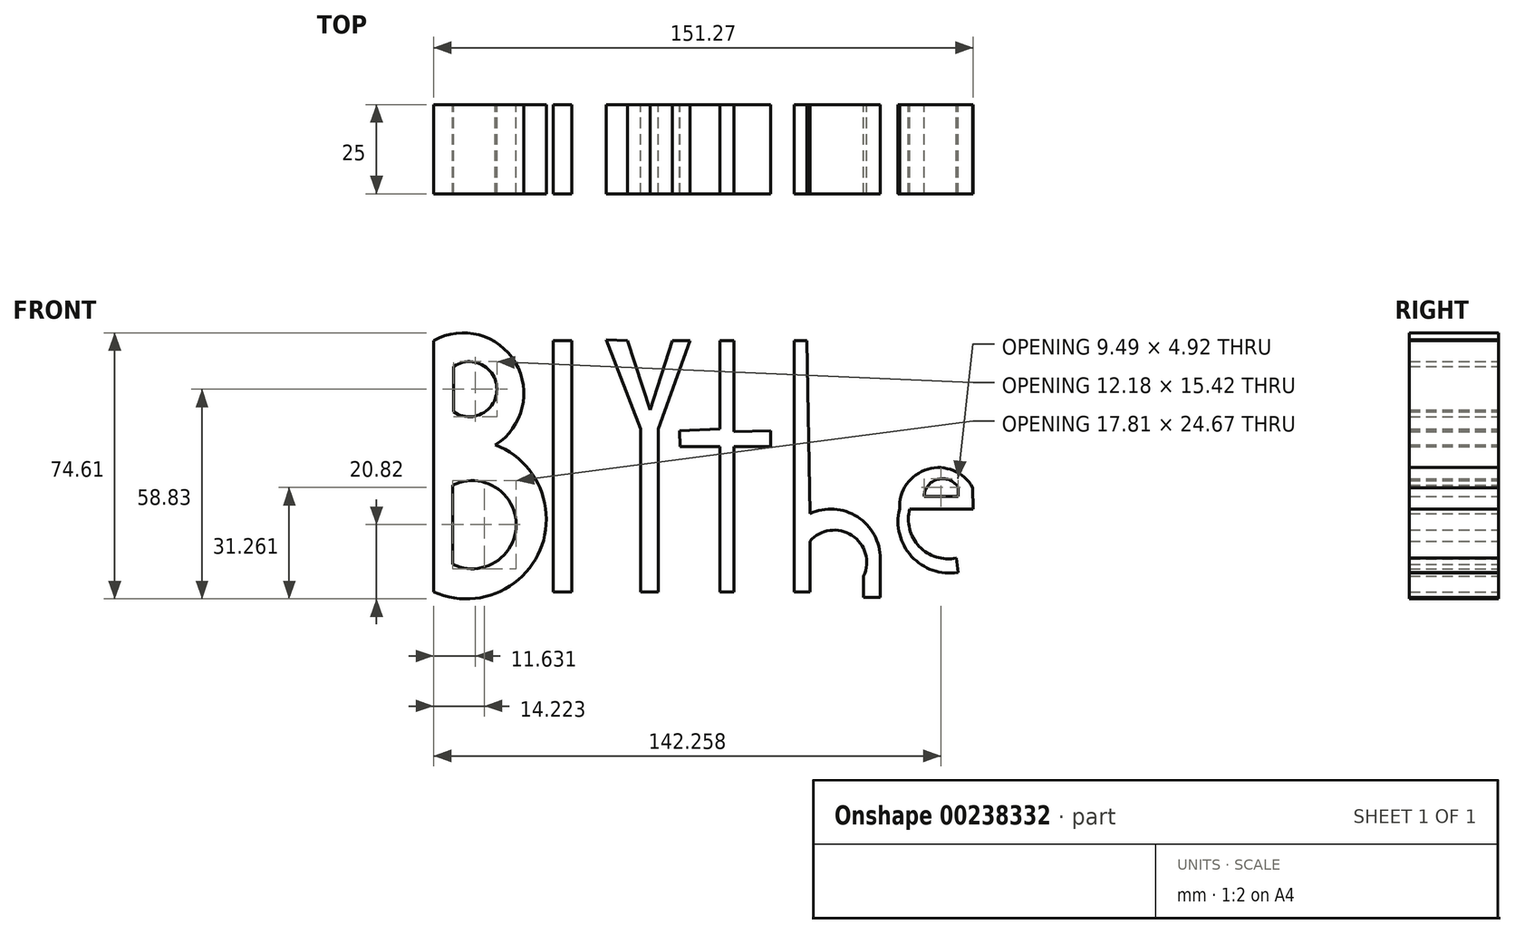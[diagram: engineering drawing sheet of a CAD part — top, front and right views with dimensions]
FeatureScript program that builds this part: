
annotation { "Feature Type Name" : "Feature", "Feature Type Description" : "" }
export const myFeature = defineFeature(function(context is Context, id is Id, definition is map)
    precondition{}
    {
        {
            var Q0;
            Q0=qCreatedBy(makeId("Front.planeOp"),FACE);
            var sketch = newSketch(context, id + "F0", { "sketchPlane" : qUnion([Q0])});
            skLineSegment(sketch, "E0", {"start": v(-71.8, 43.66) * mm, "end": v(-71.8, -26.82) * mm});
            skArc(sketch, "E1", {"start": v(-71.8, -26.82) * mm, "mid": v(-40.23, -6.43) * mm, "end": v(-71.8, 13.96) * mm});
            skArc(sketch, "E2", {"start": v(-71.8, 13.96) * mm, "mid": v(-46.53, 28.81) * mm, "end": v(-71.8, 43.66) * mm});
            skLineSegment(sketch, "E3", {"start": v(-66.27, 36.35) * mm, "end": v(-66.27, 23.71) * mm});
            skArc(sketch, "E4", {"start": v(-66.27, 23.71) * mm, "mid": v(-54.09, 30.03) * mm, "end": v(-66.27, 36.35) * mm});
            skLineSegment(sketch, "E5", {"start": v(-66.5, 3.1) * mm, "end": v(-66.5, -19.06) * mm});
            skArc(sketch, "E6", {"start": v(-66.5, -19.06) * mm, "mid": v(-48.68, -7.98) * mm, "end": v(-66.5, 3.1) * mm});
            skLineSegment(sketch, "E7", {"start": v(-38.34, 43.66) * mm, "end": v(-38.34, -26.82) * mm});
            skLineSegment(sketch, "E8", {"start": v(-38.34, -26.82) * mm, "end": v(-33.02, -26.82) * mm});
            skLineSegment(sketch, "E9", {"start": v(-33.02, -26.82) * mm, "end": v(-33.02, 43.66) * mm});
            skLineSegment(sketch, "E10", {"start": v(-33.02, 43.66) * mm, "end": v(-38.34, 43.66) * mm});
            skLineSegment(sketch, "E11", {"start": v(-17.5, 43.66) * mm, "end": v(-23.46, 43.94) * mm});
            skPoint(sketch, "E11.startSnap0", {"position": v(-35.68, 43.66) * mm});
            skLineSegment(sketch, "E12", {"start": v(-23.46, 43.94) * mm, "end": v(-13.74, 18.84) * mm});
            skLineSegment(sketch, "E13", {"start": v(-13.74, 18.84) * mm, "end": v(-13.74, -26.82) * mm});
            skLineSegment(sketch, "E14", {"start": v(-13.74, -26.82) * mm, "end": v(-8.87, -26.82) * mm});
            skLineSegment(sketch, "E15", {"start": v(-8.87, -26.82) * mm, "end": v(-8.87, 18.84) * mm});
            skLineSegment(sketch, "E16", {"start": v(-8.87, 18.84) * mm, "end": v(0, 43.66) * mm});
            skLineSegment(sketch, "E17", {"start": v(0, 43.66) * mm, "end": v(-4.88, 43.66) * mm});
            skLineSegment(sketch, "E18", {"start": v(-4.88, 43.66) * mm, "end": v(-11.08, 24.16) * mm});
            skLineSegment(sketch, "E19", {"start": v(-11.08, 24.16) * mm, "end": v(-17.5, 43.66) * mm});
            skLineSegment(sketch, "E20", {"start": v(8.42, 43.66) * mm, "end": v(8.42, 18.84) * mm});
            skLineSegment(sketch, "E21", {"start": v(8.42, 18.84) * mm, "end": v(-2.87, 18.38) * mm});
            skLineSegment(sketch, "E22", {"start": v(-2.87, 18.38) * mm, "end": v(-2.7, 13.95) * mm});
            skLineSegment(sketch, "E23", {"start": v(-2.7, 13.95) * mm, "end": v(8.42, 13.95) * mm});
            skLineSegment(sketch, "E24", {"start": v(8.42, 13.95) * mm, "end": v(8.42, -26.82) * mm});
            skLineSegment(sketch, "E25", {"start": v(8.42, -26.82) * mm, "end": v(12.41, -26.82) * mm});
            skLineSegment(sketch, "E26", {"start": v(12.41, -26.82) * mm, "end": v(12.41, 13.95) * mm});
            skLineSegment(sketch, "E27", {"start": v(12.41, 13.95) * mm, "end": v(22.6, 13.95) * mm});
            skPoint(sketch, "E27.endSnap0", {"position": v(2.86, 13.95) * mm});
            skLineSegment(sketch, "E28", {"start": v(22.6, 13.95) * mm, "end": v(22.6, 18.38) * mm});
            skLineSegment(sketch, "E29", {"start": v(22.6, 18.38) * mm, "end": v(12.41, 18.1) * mm});
            skLineSegment(sketch, "E30", {"start": v(12.41, 18.1) * mm, "end": v(12.41, 43.66) * mm});
            skLineSegment(sketch, "E31", {"start": v(12.41, 43.66) * mm, "end": v(8.42, 43.66) * mm});
            skLineSegment(sketch, "E32", {"start": v(29.26, 43.66) * mm, "end": v(29.26, -26.82) * mm});
            skLineSegment(sketch, "E33", {"start": v(29.26, -26.82) * mm, "end": v(33.69, -26.82) * mm});
            skLineSegment(sketch, "E34", {"start": v(33.69, -26.82) * mm, "end": v(33.69, -12.63) * mm});
            skArc(sketch, "E35", {"start": v(48.76, -22.39) * mm, "mid": v(45.46, -10.96) * mm, "end": v(33.69, -12.63) * mm});
            skLineSegment(sketch, "E36", {"start": v(48.76, -24.16) * mm, "end": v(48.76, -28.37) * mm});
            skLineSegment(sketch, "E37", {"start": v(48.76, -28.37) * mm, "end": v(48.76, -24.16) * mm});
            skLineSegment(sketch, "E38", {"start": v(48.76, -22.39) * mm, "end": v(48.76, -24.16) * mm});
            skLineSegment(sketch, "E39", {"start": v(48.76, -28.37) * mm, "end": v(53.41, -28.37) * mm});
            skLineSegment(sketch, "E40", {"start": v(53.41, -28.37) * mm, "end": v(53.41, -17.51) * mm});
            skArc(sketch, "E41", {"start": v(53.41, -17.51) * mm, "mid": v(47, -5.8) * mm, "end": v(33.69, -4.88) * mm});
            skLineSegment(sketch, "E42", {"start": v(29.26, 43.66) * mm, "end": v(32.8, 43.66) * mm});
            skLineSegment(sketch, "E43", {"start": v(32.8, 43.66) * mm, "end": v(33.69, -4.88) * mm});
            skLineSegment(sketch, "E44", {"start": v(58.83, -3.56) * mm, "end": v(79.46, -3.56) * mm});
            skLineSegment(sketch, "E45", {"start": v(79.46, -3.56) * mm, "end": v(79.35, 2.38) * mm});
            skArc(sketch, "E46", {"start": v(79.35, 2.38) * mm, "mid": v(66.72, 7.6) * mm, "end": v(58.83, -3.56) * mm});
            skArc(sketch, "E47", {"start": v(58.83, -3.56) * mm, "mid": v(62.2, -16.88) * mm, "end": v(75.2, -21.35) * mm});
            skArc(sketch, "E48", {"start": v(61.67, -3.56) * mm, "mid": v(64.34, -14.09) * mm, "end": v(74.72, -17.32) * mm});
            skLineSegment(sketch, "E49", {"start": v(74.72, -17.32) * mm, "end": v(75.2, -21.35) * mm});
            skLineSegment(sketch, "E50", {"start": v(65.7, 0) * mm, "end": v(75.2, 0) * mm});
            skLineSegment(sketch, "E51", {"start": v(75.2, 0) * mm, "end": v(75.2, 2.6) * mm});
            skArc(sketch, "E52", {"start": v(75.2, 2.6) * mm, "mid": v(69.5, 4.74) * mm, "end": v(65.7, 0) * mm});
            skSolve(sketch);
        }
        {
            var Q0;
            Q0=makeQuery(id+"F0.imprint","IMPRINT",FACE,{"disambiguationData":[TD([[makeQuery(id+"F0.imprint","IMPRINT",EDGE,{"derivedFrom":sQuery(id+"F0.wireOp",EDGE,"E3")}),-1.0]])]});
            var Q1;
            {var subQ0=sQuery(id+"F0.wireOp",EDGE,"E2");var subQ1=sQuery(id+"F0.wireOp",EDGE,"E1");var subQ3=makeQuery(id+"F0.imprint","INTERSECT",VERTEX,{"derivedFrom":[subQ1,subQ0]});Q1=makeQuery(id+"F0.imprint","IMPRINT",FACE,{"disambiguationData":[TD([[makeQuery(id+"F0.imprint","IMPRINT",EDGE,{"disambiguationData":[TD([[subQ3,-1.0]])],"derivedFrom":subQ1}),1.0]])]});}
            var Q2;
            Q2=makeQuery(id+"F0.imprint","IMPRINT",FACE,{"disambiguationData":[TD([[makeQuery(id+"F0.imprint","IMPRINT",EDGE,{"derivedFrom":sQuery(id+"F0.wireOp",EDGE,"E5")}),-1.0]])]});
            var Q3;
            Q3=makeQuery(id+"F0.imprint","IMPRINT",FACE,{"disambiguationData":[TD([[makeQuery(id+"F0.imprint","IMPRINT",EDGE,{"derivedFrom":sQuery(id+"F0.wireOp",EDGE,"E7")}),1.0]])]});
            var Q4;
            Q4=makeQuery(id+"F0.imprint","IMPRINT",FACE,{"disambiguationData":[TD([[makeQuery(id+"F0.imprint","IMPRINT",EDGE,{"derivedFrom":sQuery(id+"F0.wireOp",EDGE,"E11")}),1.0]])]});
            var Q5;
            Q5=makeQuery(id+"F0.imprint","IMPRINT",FACE,{"disambiguationData":[TD([[makeQuery(id+"F0.imprint","IMPRINT",EDGE,{"derivedFrom":sQuery(id+"F0.wireOp",EDGE,"E20")}),1.0]])]});
            var Q6;
            Q6=makeQuery(id+"F0.imprint","IMPRINT",FACE,{"disambiguationData":[TD([[makeQuery(id+"F0.imprint","IMPRINT",EDGE,{"derivedFrom":sQuery(id+"F0.wireOp",EDGE,"E32")}),1.0]])]});
            var Q7;
            {var subQ1=sQuery(id+"F0.wireOp",EDGE,"E45");Q7=makeQuery(id+"F0.imprint","IMPRINT",FACE,{"disambiguationData":[TD([[makeQuery(id+"F0.imprint","IMPRINT",EDGE,{"derivedFrom":subQ1}),1.0]])]});}
            var Q8;
            {var subQ0=sQuery(id+"F0.wireOp",EDGE,"E47");Q8=makeQuery(id+"F0.imprint","IMPRINT",FACE,{"disambiguationData":[TD([[makeQuery(id+"F0.imprint","IMPRINT",EDGE,{"derivedFrom":subQ0}),1.0]])]});}
            extrude(context, id + "F1", {"entities" : qUnion([Q0, Q1, Q2, Q3, Q4, Q5, Q6, Q7, Q8]), "depth" : 25 * mm});
        }
    });
